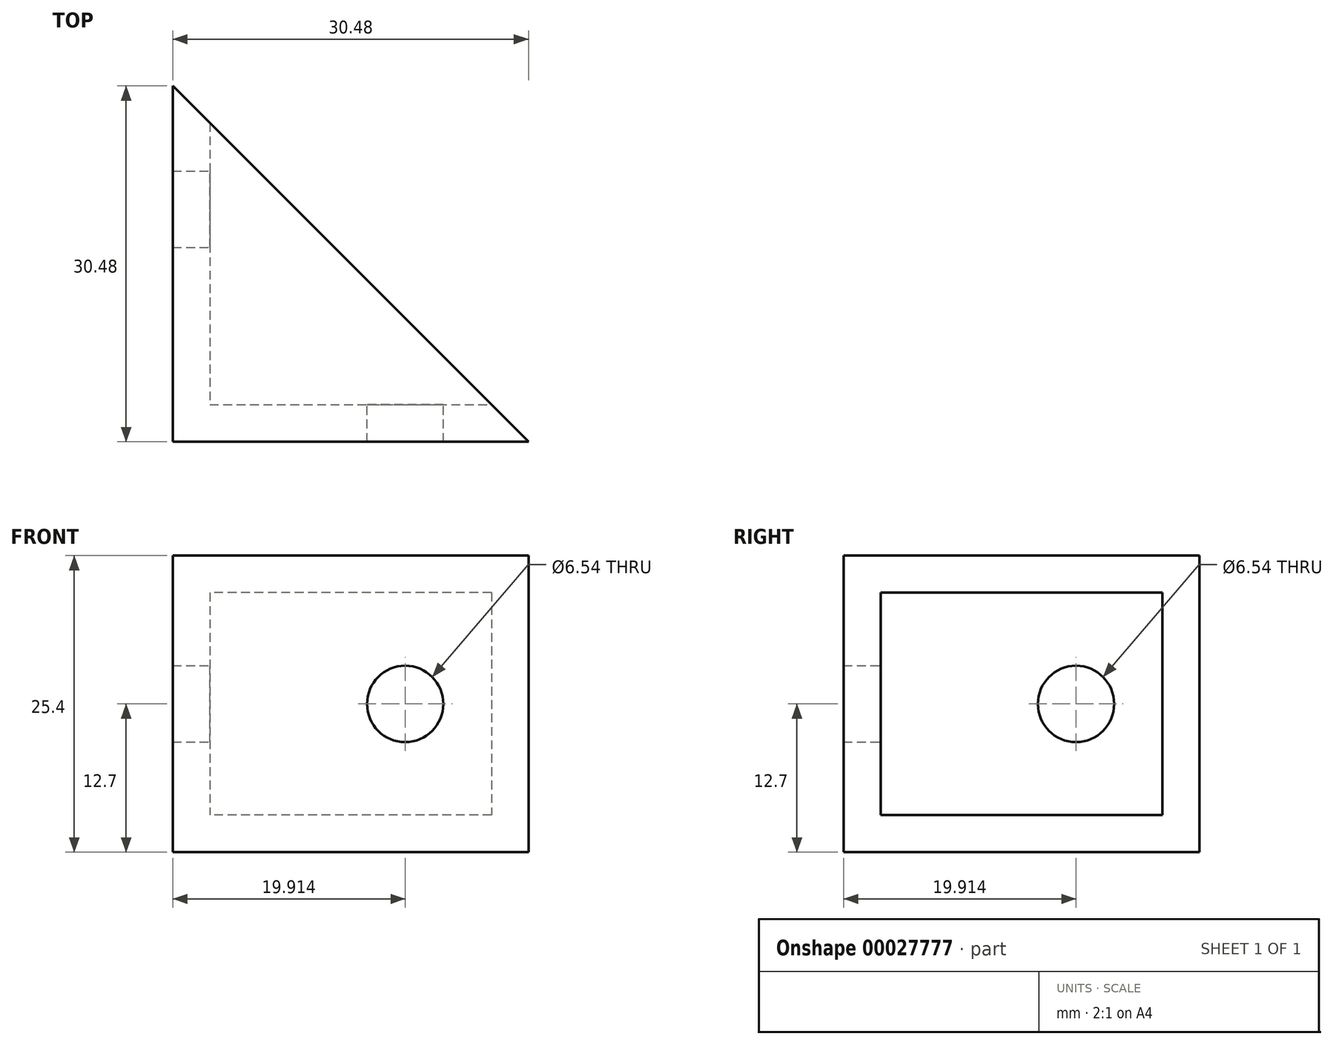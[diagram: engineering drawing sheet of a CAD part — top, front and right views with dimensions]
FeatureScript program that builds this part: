
annotation { "Feature Type Name" : "Feature", "Feature Type Description" : "" }
export const myFeature = defineFeature(function(context is Context, id is Id, definition is map)
    precondition{}
    {
        {
            var Q0;
            Q0=qCreatedBy(makeId("Top.planeOp"),FACE);
            var sketch = newSketch(context, id + "F0", { "sketchPlane" : qUnion([Q0])});
            skLineSegment(sketch, "E0", {"start": v(0, 0) * mm, "end": v(0, 30.48) * mm});
            skLineSegment(sketch, "E1", {"start": v(0, 0) * mm, "end": v(30.48, 0) * mm});
            skLineSegment(sketch, "E2", {"start": v(30.48, 0) * mm, "end": v(0, 30.48) * mm});
            skPoint(sketch, "E3", {"position": v(0, 19.91) * mm});
            skSolve(sketch);
        }
        {
            var Q0;
            Q0 = qSketchRegion(id + "F0", true);
            extrude(context, id + "F1", {"entities" : qUnion([Q0]), "depth" : 3.17 * mm});
        }
        {
            var Q0;
            Q0=makeQuery(id+"F1.opExtrude","CAP_FACE",FACE,{"disambiguationData":[OSD([sQuery(id+"F0.wireOp",EDGE,"E0"),sQuery(id+"F0.wireOp",EDGE,"E1"),sQuery(id+"F0.wireOp",EDGE,"E2")])],"isStart":false});
            var sketch = newSketch(context, id + "F2", { "sketchPlane" : qUnion([Q0])});
            skLineSegment(sketch, "E4", {"start": v(3.18, 27.3) * mm, "end": v(3.18, 0) * mm});
            skPoint(sketch, "E5", {"position": v(0, 27.3) * mm});
            skLineSegment(sketch, "E6", {"start": v(0, 3.18) * mm, "end": v(27.3, 3.18) * mm});
            skSolve(sketch);
        }
        {
            var Q0;
            {var subQ0=makeQuery(id+"F1.opExtrude","CAP_EDGE",EDGE,{"disambiguationData":[OSD([sQuery(id+"F0.wireOp",EDGE,"E2")])],"isStart":false});var subQ1=sQuery(id+"F2.wireOp",EDGE,"E4");var subQ2=makeQuery(id+"F2.imprint","INTERSECT",VERTEX,{"derivedFrom":[subQ0,subQ1]});Q0=makeQuery(id+"F2.imprint","IMPRINT",FACE,{"disambiguationData":[TD([[makeQuery(id+"F2.imprint","IMPRINT",EDGE,{"disambiguationData":[TD([[subQ2,-1.0]])],"derivedFrom":subQ1}),-1.0]])]});}
            var Q1;
            {var subQ3=makeQuery(id+"F1.opExtrude","CAP_EDGE",EDGE,{"disambiguationData":[OSD([sQuery(id+"F0.wireOp",EDGE,"E1")])],"isStart":false});var subQ5=sQuery(id+"F2.wireOp",EDGE,"E4");var subQ7=makeQuery(id+"F2.imprint","INTERSECT",VERTEX,{"derivedFrom":[subQ3,subQ5]});Q1=makeQuery(id+"F2.imprint","IMPRINT",FACE,{"disambiguationData":[TD([[makeQuery(id+"F2.imprint","IMPRINT",EDGE,{"disambiguationData":[TD([[subQ7,1.0]])],"derivedFrom":subQ5}),-1.0]])]});}
            var Q2;
            {var subQ3=makeQuery(id+"F1.opExtrude","CAP_EDGE",EDGE,{"disambiguationData":[OSD([sQuery(id+"F0.wireOp",EDGE,"E1")])],"isStart":false});var subQ5=sQuery(id+"F2.wireOp",EDGE,"E4");var subQ6=makeQuery(id+"F2.imprint","INTERSECT",VERTEX,{"derivedFrom":[subQ3,subQ5]});Q2=makeQuery(id+"F2.imprint","IMPRINT",FACE,{"disambiguationData":[TD([[makeQuery(id+"F2.imprint","IMPRINT",EDGE,{"disambiguationData":[TD([[subQ6,1.0]])],"derivedFrom":subQ5}),1.0]])]});}
            extrude(context, id + "F3", {"entities" : qUnion([Q0, Q1, Q2]), "operationType" : NewBodyOperationType.ADD, "depth" : 19.05 * mm});
        }
        {
            var Q0;
            Q0=makeQuery(id+"F3.opExtrude","CAP_FACE",FACE,{"disambiguationData":[OSD([sQuery(id+"F0.wireOp",EDGE,"E0"),sQuery(id+"F0.wireOp",EDGE,"E1"),sQuery(id+"F0.wireOp",EDGE,"E2"),sQuery(id+"F2.wireOp",EDGE,"E4"),sQuery(id+"F2.wireOp",EDGE,"E6")])],"isStart":false});
            var sketch = newSketch(context, id + "F4", { "sketchPlane" : qUnion([Q0])});
            skLineSegment(sketch, "E7", {"start": v(0, 30.48) * mm, "end": v(30.48, 0) * mm});
            skLineSegment(sketch, "E8", {"start": v(30.48, 0) * mm, "end": v(0, 0) * mm});
            skLineSegment(sketch, "E9", {"start": v(0, 0) * mm, "end": v(0, 30.48) * mm});
            skSolve(sketch);
        }
        {
            var Q0;
            Q0 = qSketchRegion(id + "F4", true);
            extrude(context, id + "F5", {"entities" : qUnion([Q0]), "operationType" : NewBodyOperationType.ADD, "depth" : 3.17 * mm});
        }
        {
            var Q0;
            Q0=makeQuery(id+"F3.opExtrude","SWEPT_FACE",FACE,{"disambiguationData":[OSD([sQuery(id+"F2.wireOp",EDGE,"E4")])]});
            var sketch = newSketch(context, id + "F6", { "sketchPlane" : qUnion([Q0])});
            skLineSegment(sketch, "E10.bottom", {"start": v(3.18, 22.23) * mm, "end": v(27.3, 22.23) * mm});
            skLineSegment(sketch, "E10.top", {"start": v(3.18, 3.18) * mm, "end": v(27.3, 3.18) * mm});
            skLineSegment(sketch, "E10.left", {"start": v(3.18, 22.23) * mm, "end": v(3.18, 3.18) * mm});
            skLineSegment(sketch, "E10.right", {"start": v(27.3, 22.23) * mm, "end": v(27.3, 3.18) * mm});
            skLineSegment(sketch, "E11", {"start": v(19.91, 12.7) * mm, "end": v(19.91, 12.7) * mm});
            skLineSegment(sketch, "E12.rect.bottom", {"start": v(22.23, 10.39) * mm, "end": v(17.6, 10.39) * mm});
            skLineSegment(sketch, "E12.rect.top", {"start": v(22.23, 15.01) * mm, "end": v(17.6, 15.01) * mm});
            skLineSegment(sketch, "E12.rect.left", {"start": v(22.23, 10.39) * mm, "end": v(22.23, 15.01) * mm});
            skLineSegment(sketch, "E12.rect.right", {"start": v(17.6, 10.39) * mm, "end": v(17.6, 15.01) * mm});
            skPoint(sketch, "E12.rect.middle", {"position": v(19.91, 12.7) * mm});
            skCircle(sketch, "E13", {"center": v(19.91, 12.7) * mm, "radius": 3.27 * mm});
            skSolve(sketch);
        }
        {
            var Q0;
            Q0=makeQuery(id+"F3.opExtrude","SWEPT_FACE",FACE,{"disambiguationData":[OSD([sQuery(id+"F2.wireOp",EDGE,"E6")])]});
            var sketch = newSketch(context, id + "F7", { "sketchPlane" : qUnion([Q0])});
            skLineSegment(sketch, "E14.bottom", {"start": v(-27.3, 3.18) * mm, "end": v(-3.18, 3.18) * mm});
            skLineSegment(sketch, "E14.top", {"start": v(-27.3, 22.23) * mm, "end": v(-3.18, 22.23) * mm});
            skLineSegment(sketch, "E14.left", {"start": v(-27.3, 3.18) * mm, "end": v(-27.3, 22.23) * mm});
            skLineSegment(sketch, "E14.right", {"start": v(-3.18, 3.18) * mm, "end": v(-3.18, 22.23) * mm});
            skLineSegment(sketch, "E15", {"start": v(-3.18, 12.7) * mm, "end": v(-19.91, 12.7) * mm});
            skLineSegment(sketch, "E16.rect.bottom", {"start": v(-22.23, 10.39) * mm, "end": v(-17.6, 10.39) * mm});
            skLineSegment(sketch, "E16.rect.top", {"start": v(-22.23, 15.01) * mm, "end": v(-17.6, 15.01) * mm});
            skLineSegment(sketch, "E16.rect.left", {"start": v(-22.23, 10.39) * mm, "end": v(-22.23, 15.01) * mm});
            skLineSegment(sketch, "E16.rect.right", {"start": v(-17.6, 10.39) * mm, "end": v(-17.6, 15.01) * mm});
            skPoint(sketch, "E16.rect.middle", {"position": v(-19.91, 12.7) * mm});
            skCircle(sketch, "E17", {"center": v(-19.91, 12.7) * mm, "radius": 3.27 * mm});
            skSolve(sketch);
        }
        {
            var Q0;
            {var subQ3=sQuery(id+"F7.wireOp",EDGE,"E16.rect.bottom");Q0=makeQuery(id+"F7.imprint","IMPRINT",FACE,{"disambiguationData":[TD([[makeQuery(id+"F7.imprint","IMPRINT",EDGE,{"derivedFrom":subQ3}),1.0]])]});}
            var Q1;
            {var subQ1=sQuery(id+"F7.wireOp",EDGE,"E16.rect.left");Q1=makeQuery(id+"F7.imprint","IMPRINT",FACE,{"disambiguationData":[TD([[makeQuery(id+"F7.imprint","IMPRINT",EDGE,{"derivedFrom":subQ1}),1.0]])]});}
            var Q2;
            {var subQ1=sQuery(id+"F7.wireOp",EDGE,"E16.rect.top");Q2=makeQuery(id+"F7.imprint","IMPRINT",FACE,{"disambiguationData":[TD([[makeQuery(id+"F7.imprint","IMPRINT",EDGE,{"derivedFrom":subQ1}),1.0]])]});}
            var Q3;
            {var subQ1=sQuery(id+"F7.wireOp",EDGE,"E15");var subQ3=sQuery(id+"F7.wireOp",EDGE,"E16.rect.right");var subQ5=makeQuery(id+"F7.imprint","INTERSECT",VERTEX,{"derivedFrom":[subQ1,subQ3]});Q3=makeQuery(id+"F7.imprint","IMPRINT",FACE,{"disambiguationData":[TD([[makeQuery(id+"F7.imprint","IMPRINT",EDGE,{"disambiguationData":[TD([[subQ5,1.0]])],"derivedFrom":subQ1}),-1.0]])]});}
            var Q4;
            {var subQ1=sQuery(id+"F7.wireOp",EDGE,"E16.rect.bottom");Q4=makeQuery(id+"F7.imprint","IMPRINT",FACE,{"disambiguationData":[TD([[makeQuery(id+"F7.imprint","IMPRINT",EDGE,{"derivedFrom":subQ1}),-1.0]])]});}
            var Q5;
            {var subQ1=sQuery(id+"F7.wireOp",EDGE,"E15");var subQ3=sQuery(id+"F7.wireOp",EDGE,"E16.rect.right");var subQ5=makeQuery(id+"F7.imprint","INTERSECT",VERTEX,{"derivedFrom":[subQ1,subQ3]});Q5=makeQuery(id+"F7.imprint","IMPRINT",FACE,{"disambiguationData":[TD([[makeQuery(id+"F7.imprint","IMPRINT",EDGE,{"disambiguationData":[TD([[subQ5,1.0]])],"derivedFrom":subQ1}),1.0]])]});}
            extrude(context, id + "F8", {"entities" : qUnion([Q0, Q1, Q2, Q3, Q4, Q5]), "operationType" : NewBodyOperationType.REMOVE, "oppositeDirection" : true, "depth" : 25.4 * mm});
        }
        {
            var Q0;
            Q0=makeQuery(id+"F6.imprint","IMPRINT",FACE,{"disambiguationData":[TD([[makeQuery(id+"F6.imprint","IMPRINT",EDGE,{"derivedFrom":sQuery(id+"F6.wireOp",EDGE,"E12.rect.bottom")}),-1.0]])]});
            var Q1;
            {var subQ1=sQuery(id+"F6.wireOp",EDGE,"E12.rect.right");Q1=makeQuery(id+"F6.imprint","IMPRINT",FACE,{"disambiguationData":[TD([[makeQuery(id+"F6.imprint","IMPRINT",EDGE,{"derivedFrom":subQ1}),1.0]])]});}
            var Q2;
            {var subQ1=sQuery(id+"F6.wireOp",EDGE,"E12.rect.top");Q2=makeQuery(id+"F6.imprint","IMPRINT",FACE,{"disambiguationData":[TD([[makeQuery(id+"F6.imprint","IMPRINT",EDGE,{"derivedFrom":subQ1}),-1.0]])]});}
            var Q3;
            {var subQ1=sQuery(id+"F6.wireOp",EDGE,"E12.rect.left");Q3=makeQuery(id+"F6.imprint","IMPRINT",FACE,{"disambiguationData":[TD([[makeQuery(id+"F6.imprint","IMPRINT",EDGE,{"derivedFrom":subQ1}),-1.0]])]});}
            var Q4;
            {var subQ1=sQuery(id+"F6.wireOp",EDGE,"E12.rect.bottom");Q4=makeQuery(id+"F6.imprint","IMPRINT",FACE,{"disambiguationData":[TD([[makeQuery(id+"F6.imprint","IMPRINT",EDGE,{"derivedFrom":subQ1}),1.0]])]});}
            extrude(context, id + "F9", {"entities" : qUnion([Q0, Q1, Q2, Q3, Q4]), "operationType" : NewBodyOperationType.REMOVE, "oppositeDirection" : true, "depth" : 25.4 * mm});
        }
    });
